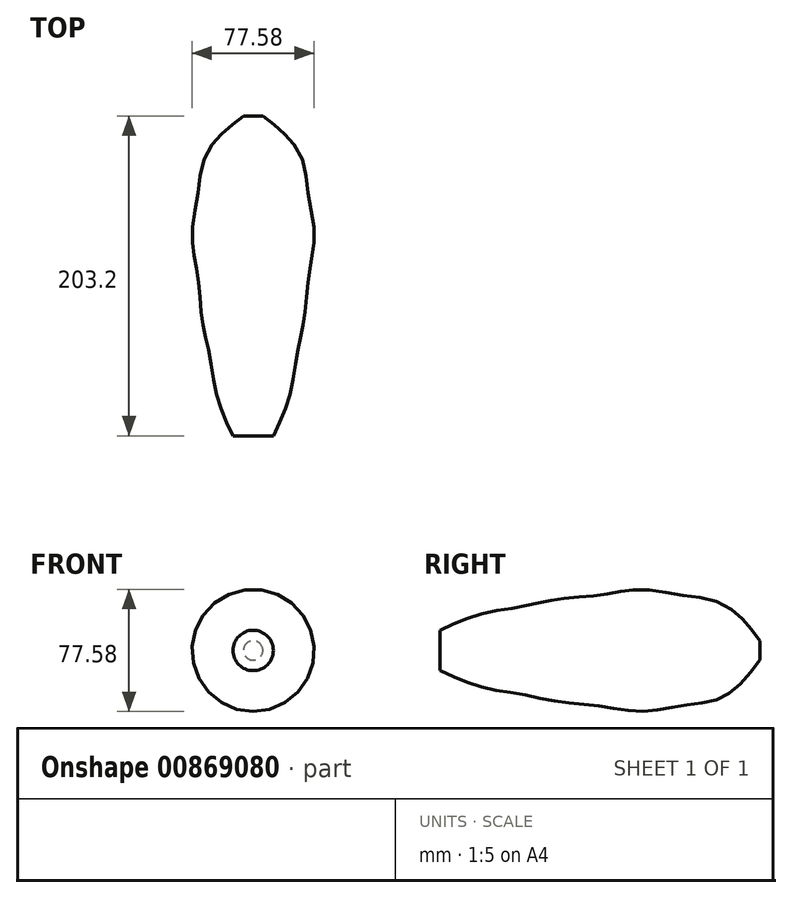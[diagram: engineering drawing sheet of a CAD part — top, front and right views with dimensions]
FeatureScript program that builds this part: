
annotation { "Feature Type Name" : "Feature", "Feature Type Description" : "" }
export const myFeature = defineFeature(function(context is Context, id is Id, definition is map)
    precondition{}
    {
        {
            var Q0;
            Q0=qCreatedBy(makeId("Front.planeOp"),FACE);
            var sketch = newSketch(context, id + "F0", { "sketchPlane" : qUnion([Q0])});
            skCircle(sketch, "E0", {"center": v(0, 0) * mm, "radius": 38.8 * mm});
            skSolve(sketch);
        }
        {
            var Q0;
            Q0=qCreatedBy(makeId("Front.planeOp"),FACE);
            cPlane(context, id + "F1", {"entities" : qUnion([Q0]), "cplaneType" : CPlaneType.OFFSET, "offset" : 25.4 * mm, "width" : 152.4 * mm, "height" : 152.4 * mm});
        }
        {
            var Q0;
            Q0=qCreatedBy(id+"F1.planeOp",FACE);
            cPlane(context, id + "F2", {"entities" : qUnion([Q0]), "cplaneType" : CPlaneType.OFFSET, "offset" : 25.4 * mm, "width" : 152.4 * mm, "height" : 152.4 * mm});
        }
        {
            var Q0;
            Q0=qCreatedBy(id+"F2.planeOp",FACE);
            cPlane(context, id + "F3", {"entities" : qUnion([Q0]), "cplaneType" : CPlaneType.OFFSET, "offset" : 25.4 * mm, "width" : 152.4 * mm, "height" : 152.4 * mm});
        }
        {
            var Q0;
            Q0=qCreatedBy(id+"F3.planeOp",FACE);
            cPlane(context, id + "F4", {"entities" : qUnion([Q0]), "cplaneType" : CPlaneType.OFFSET, "offset" : 25.4 * mm, "width" : 152.4 * mm, "height" : 152.4 * mm});
        }
        {
            var Q0;
            Q0=qCreatedBy(id+"F4.planeOp",FACE);
            cPlane(context, id + "F5", {"entities" : qUnion([Q0]), "cplaneType" : CPlaneType.OFFSET, "offset" : 25.4 * mm, "width" : 152.4 * mm, "height" : 152.4 * mm});
        }
        {
            var Q0;
            Q0=qCreatedBy(makeId("Front.planeOp"),FACE);
            cPlane(context, id + "F6", {"entities" : qUnion([Q0]), "cplaneType" : CPlaneType.OFFSET, "offset" : 25.4 * mm, "oppositeDirection" : true, "width" : 152.4 * mm, "height" : 152.4 * mm});
        }
        {
            var Q0;
            Q0=qCreatedBy(id+"F6.planeOp",FACE);
            cPlane(context, id + "F7", {"entities" : qUnion([Q0]), "cplaneType" : CPlaneType.OFFSET, "offset" : 25.4 * mm, "oppositeDirection" : true, "width" : 152.4 * mm, "height" : 152.4 * mm});
        }
        {
            var Q0;
            Q0=qCreatedBy(id+"F7.planeOp",FACE);
            cPlane(context, id + "F8", {"entities" : qUnion([Q0]), "cplaneType" : CPlaneType.OFFSET, "offset" : 25.4 * mm, "oppositeDirection" : true, "width" : 152.4 * mm, "height" : 152.4 * mm});
        }
        {
            var Q0;
            Q0=qCreatedBy(id+"F1.planeOp",FACE);
            var sketch = newSketch(context, id + "F9", { "sketchPlane" : qUnion([Q0])});
            skCircle(sketch, "E1", {"center": v(0, 0) * mm, "radius": 35.2 * mm});
            skSolve(sketch);
        }
        {
            var Q0;
            Q0=qCreatedBy(id+"F2.planeOp",FACE);
            var sketch = newSketch(context, id + "F10", { "sketchPlane" : qUnion([Q0])});
            skCircle(sketch, "E2", {"center": v(0, 0) * mm, "radius": 32.7 * mm});
            skSolve(sketch);
        }
        {
            var Q0;
            Q0=qCreatedBy(id+"F3.planeOp",FACE);
            var sketch = newSketch(context, id + "F11", { "sketchPlane" : qUnion([Q0])});
            skCircle(sketch, "E3", {"center": v(0, 0) * mm, "radius": 27.72 * mm});
            skSolve(sketch);
        }
        {
            var Q0;
            Q0=qCreatedBy(id+"F4.planeOp",FACE);
            var sketch = newSketch(context, id + "F12", { "sketchPlane" : qUnion([Q0])});
            skCircle(sketch, "E4", {"center": v(0, 0) * mm, "radius": 23.06 * mm});
            skSolve(sketch);
        }
        {
            var Q0;
            Q0=qCreatedBy(id+"F5.planeOp",FACE);
            var sketch = newSketch(context, id + "F13", { "sketchPlane" : qUnion([Q0])});
            skCircle(sketch, "E5", {"center": v(0, 0) * mm, "radius": 12.82 * mm});
            skSolve(sketch);
        }
        {
            var Q0;
            Q0=qCreatedBy(id+"F6.planeOp",FACE);
            var sketch = newSketch(context, id + "F14", { "sketchPlane" : qUnion([Q0])});
            skCircle(sketch, "E6", {"center": v(0, 0) * mm, "radius": 35.28 * mm});
            skSolve(sketch);
        }
        {
            var Q0;
            Q0=qCreatedBy(id+"F7.planeOp",FACE);
            var sketch = newSketch(context, id + "F15", { "sketchPlane" : qUnion([Q0])});
            skCircle(sketch, "E7", {"center": v(0, 0) * mm, "radius": 30.34 * mm});
            skSolve(sketch);
        }
        {
            var Q0;
            Q0=qCreatedBy(id+"F8.planeOp",FACE);
            var sketch = newSketch(context, id + "F16", { "sketchPlane" : qUnion([Q0])});
            skCircle(sketch, "E8", {"center": v(0, 0) * mm, "radius": 6.16 * mm});
            skSolve(sketch);
        }
        {
            var Q0;
            Q0=makeQuery(id+"F16.imprint","IMPRINT",FACE,{"disambiguationData":[TD([[makeQuery(id+"F16.imprint","IMPRINT",EDGE,{"derivedFrom":sQuery(id+"F16.wireOp",EDGE,"E8")}),1.0]])]});
            var Q1;
            Q1=makeQuery(id+"F15.imprint","IMPRINT",FACE,{"disambiguationData":[TD([[makeQuery(id+"F15.imprint","IMPRINT",EDGE,{"derivedFrom":sQuery(id+"F15.wireOp",EDGE,"E7")}),1.0]])]});
            var Q2;
            Q2=makeQuery(id+"F14.imprint","IMPRINT",FACE,{"disambiguationData":[TD([[makeQuery(id+"F14.imprint","IMPRINT",EDGE,{"derivedFrom":sQuery(id+"F14.wireOp",EDGE,"E6")}),1.0]])]});
            var Q3;
            Q3=makeQuery(id+"F0.imprint","IMPRINT",FACE,{"disambiguationData":[TD([[makeQuery(id+"F0.imprint","IMPRINT",EDGE,{"derivedFrom":sQuery(id+"F0.wireOp",EDGE,"E0")}),1.0]])]});
            var Q4;
            Q4=makeQuery(id+"F9.imprint","IMPRINT",FACE,{"disambiguationData":[TD([[makeQuery(id+"F9.imprint","IMPRINT",EDGE,{"derivedFrom":sQuery(id+"F9.wireOp",EDGE,"E1")}),1.0]])]});
            var Q5;
            Q5=makeQuery(id+"F10.imprint","IMPRINT",FACE,{"disambiguationData":[TD([[makeQuery(id+"F10.imprint","IMPRINT",EDGE,{"derivedFrom":sQuery(id+"F10.wireOp",EDGE,"E2")}),1.0]])]});
            var Q6;
            Q6=makeQuery(id+"F11.imprint","IMPRINT",FACE,{"disambiguationData":[TD([[makeQuery(id+"F11.imprint","IMPRINT",EDGE,{"derivedFrom":sQuery(id+"F11.wireOp",EDGE,"E3")}),1.0]])]});
            var Q7;
            Q7=makeQuery(id+"F12.imprint","IMPRINT",FACE,{"disambiguationData":[TD([[makeQuery(id+"F12.imprint","IMPRINT",EDGE,{"derivedFrom":sQuery(id+"F12.wireOp",EDGE,"E4")}),1.0]])]});
            var Q8;
            Q8=makeQuery(id+"F13.imprint","IMPRINT",FACE,{"disambiguationData":[TD([[makeQuery(id+"F13.imprint","IMPRINT",EDGE,{"derivedFrom":sQuery(id+"F13.wireOp",EDGE,"E5")}),1.0]])]});
            loft(context, id + "F17", {"sheetProfilesArray" : [{ "sheetProfileEntities" : qUnion([Q0]) }, { "sheetProfileEntities" : qUnion([Q1]) }, { "sheetProfileEntities" : qUnion([Q2]) }, { "sheetProfileEntities" : qUnion([Q3]) }, { "sheetProfileEntities" : qUnion([Q4]) }, { "sheetProfileEntities" : qUnion([Q5]) }, { "sheetProfileEntities" : qUnion([Q6]) }, { "sheetProfileEntities" : qUnion([Q7]) }, { "sheetProfileEntities" : qUnion([Q8]) }]});
        }
    });
